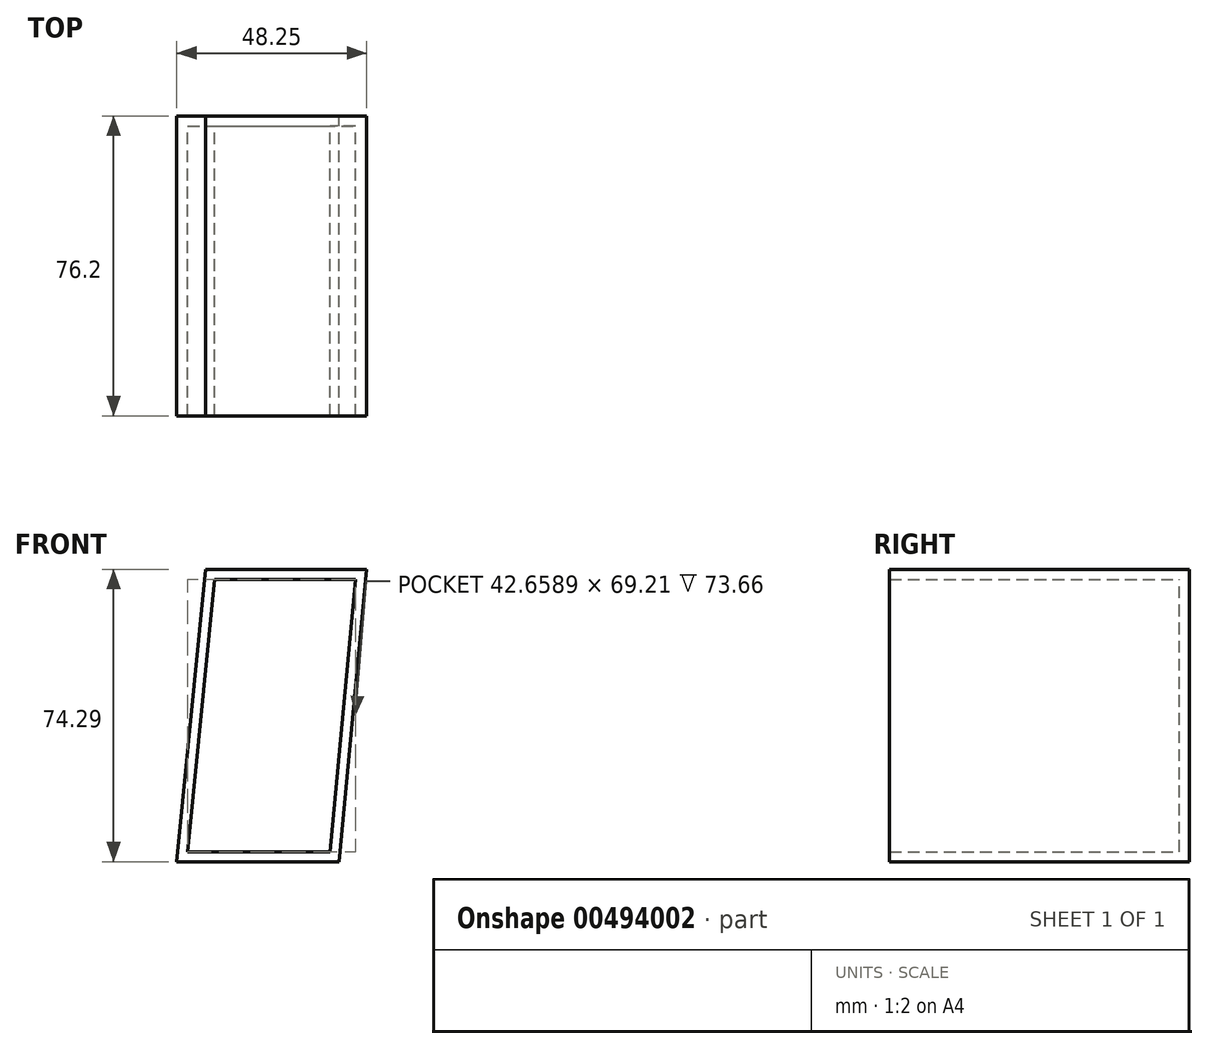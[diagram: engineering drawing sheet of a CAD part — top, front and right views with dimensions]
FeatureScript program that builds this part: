
annotation { "Feature Type Name" : "Feature", "Feature Type Description" : "" }
export const myFeature = defineFeature(function(context is Context, id is Id, definition is map)
    precondition{}
    {
        {
            var Q0;
            Q0=qCreatedBy(makeId("Front.planeOp"),FACE);
            var sketch = newSketch(context, id + "F0", { "sketchPlane" : qUnion([Q0])});
            skLineSegment(sketch, "E0.bottom", {"start": v(-17.53, 65.27) * mm, "end": v(23.37, 65.27) * mm});
            skLineSegment(sketch, "E0.top", {"start": v(-24.88, -9.02) * mm, "end": v(16.42, -9.02) * mm});
            skLineSegment(sketch, "E1", {"start": v(-24.88, -9.02) * mm, "end": v(-17.53, 65.27) * mm});
            skLineSegment(sketch, "E2", {"start": v(23.37, 65.27) * mm, "end": v(16.42, -9.02) * mm});
            skLineSegment(sketch, "E3", {"start": v(-17.53, 65.27) * mm, "end": v(-17.53, -9.02) * mm});
            skLineSegment(sketch, "E4", {"start": v(16.42, -9.02) * mm, "end": v(16.42, 65.27) * mm});
            skSolve(sketch);
        }
        {
            var Q0;
            {var subQ0=sQuery(id+"F0.wireOp",EDGE,"E1");Q0=makeQuery(id+"F0.imprint","IMPRINT",FACE,{"disambiguationData":[TD([[makeQuery(id+"F0.imprint","IMPRINT",EDGE,{"derivedFrom":subQ0}),-1.0]])]});}
            var Q1;
            {var subQ0=sQuery(id+"F0.wireOp",EDGE,"E3");Q1=makeQuery(id+"F0.imprint","IMPRINT",FACE,{"disambiguationData":[TD([[makeQuery(id+"F0.imprint","IMPRINT",EDGE,{"derivedFrom":subQ0}),1.0]])]});}
            var Q2;
            {var subQ0=sQuery(id+"F0.wireOp",EDGE,"E2");Q2=makeQuery(id+"F0.imprint","IMPRINT",FACE,{"disambiguationData":[TD([[makeQuery(id+"F0.imprint","IMPRINT",EDGE,{"derivedFrom":subQ0}),-1.0]])]});}
            extrude(context, id + "F1", {"entities" : qUnion([Q0, Q1, Q2]), "depth" : 76.2 * mm});
        }
        {
            var Q0;
            Q0=makeQuery(id+"F1.opExtrude","CAP_FACE",FACE,{"disambiguationData":[OSD([sQuery(id+"F0.wireOp",EDGE,"E0.bottom"),sQuery(id+"F0.wireOp",EDGE,"E0.top"),sQuery(id+"F0.wireOp",EDGE,"E1"),sQuery(id+"F0.wireOp",EDGE,"E2")])],"isStart":false});
            shell(context, id + "F2", {"entities" : qUnion([Q0]), "thickness" : 2.54 * mm});
        }
    });
